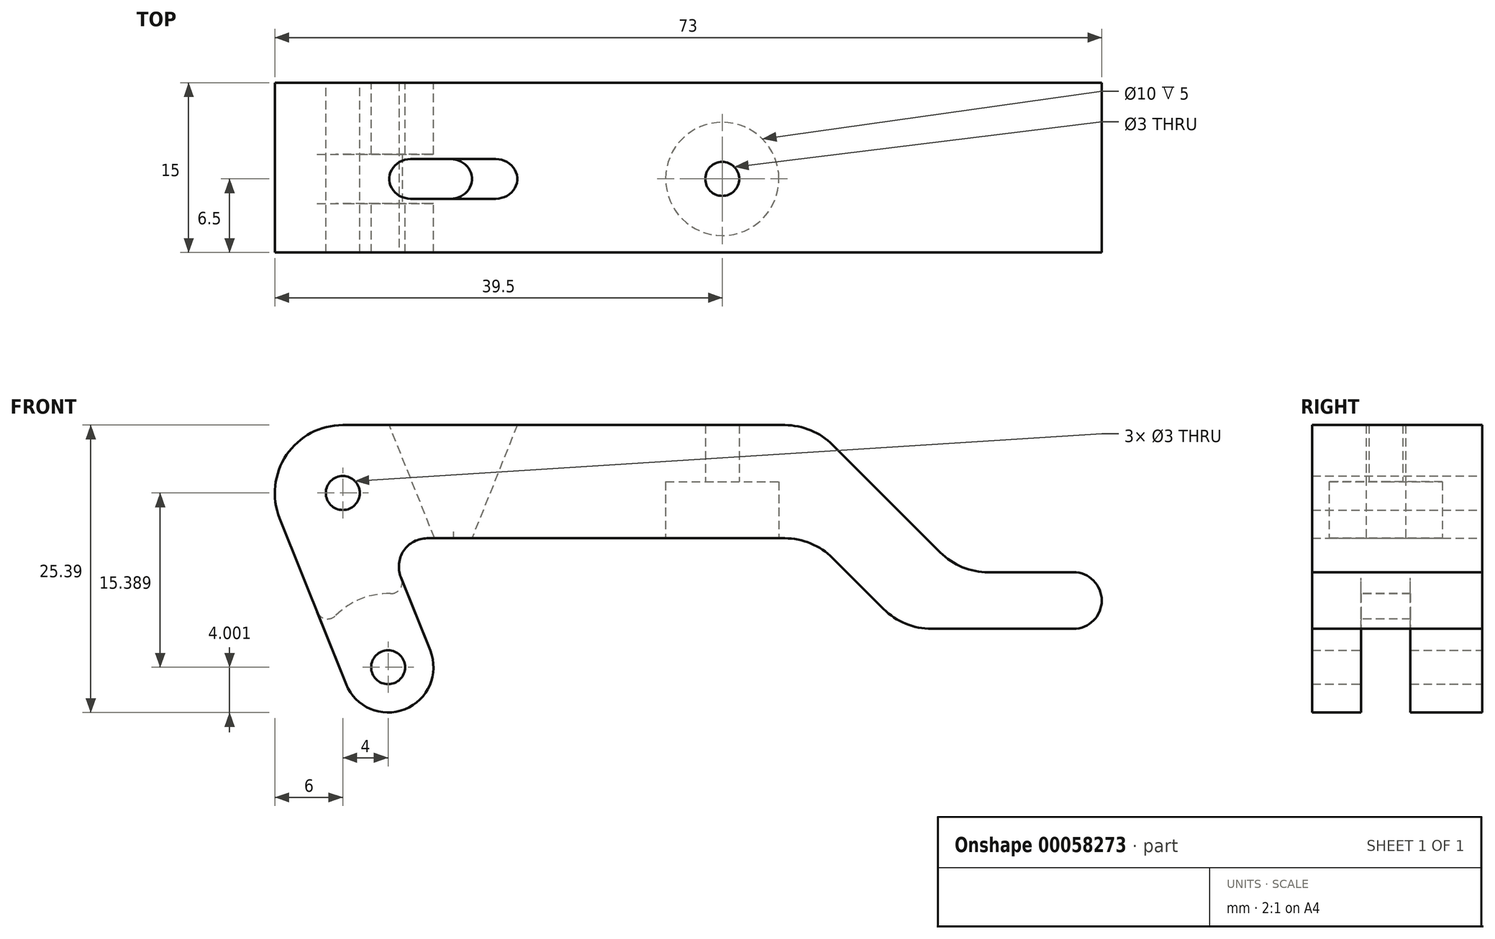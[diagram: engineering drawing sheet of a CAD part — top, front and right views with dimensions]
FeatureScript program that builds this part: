
annotation { "Feature Type Name" : "Feature", "Feature Type Description" : "" }
export const myFeature = defineFeature(function(context is Context, id is Id, definition is map)
    precondition{}
    {
        {
            var Q0;
            Q0=qCreatedBy(makeId("Front.planeOp"),FACE);
            var sketch = newSketch(context, id + "F0", { "sketchPlane" : qUnion([Q0])});
            skLineSegment(sketch, "E0", {"start": v(0, 0) * mm, "end": v(31, 0) * mm, "construction": true});
            skCircle(sketch, "E1", {"center": v(0, 0) * mm, "radius": 1.5 * mm});
            skLineSegment(sketch, "E2", {"start": v(0, 0) * mm, "end": v(4, -15.39) * mm, "construction": true});
            skCircle(sketch, "E3", {"center": v(4, -15.39) * mm, "radius": 1.5 * mm});
            skArc(sketch, "E4", {"start": v(-5.57, -2.23) * mm, "mid": v(-4.97, 3.36) * mm, "end": v(0, 6) * mm});
            skArc(sketch, "E5", {"start": v(0.29, -16.87) * mm, "mid": v(5.49, -19.1) * mm, "end": v(7.71, -13.9) * mm});
            skLineSegment(sketch, "E6", {"start": v(-5.57, -2.23) * mm, "end": v(0.29, -16.87) * mm});
            skLineSegment(sketch, "E7", {"start": v(0, 6) * mm, "end": v(41.5, 6) * mm});
            skLineSegment(sketch, "E8", {"start": v(41.5, 6) * mm, "end": v(54.5, -7) * mm});
            skLineSegment(sketch, "E9", {"start": v(54.5, -7) * mm, "end": v(67, -7) * mm});
            skLineSegment(sketch, "E10", {"start": v(15.5, 0) * mm, "end": v(15.5, -12.95) * mm, "construction": true});
            skLineSegment(sketch, "E11", {"start": v(9.75, 0) * mm, "end": v(9.75, -27.58) * mm, "construction": true});
            skLineSegment(sketch, "E12", {"start": v(7.71, -13.9) * mm, "end": v(3.75, -4) * mm});
            skLineSegment(sketch, "E13", {"start": v(3.75, -4) * mm, "end": v(41.5, -4) * mm});
            skLineSegment(sketch, "E14", {"start": v(41.5, -4) * mm, "end": v(49.5, -12) * mm});
            skLineSegment(sketch, "E15", {"start": v(49.5, -12) * mm, "end": v(67, -12) * mm});
            skLineSegment(sketch, "E16", {"start": v(67, -12) * mm, "end": v(67, -7) * mm});
            skSolve(sketch);
        }
        {
            var Q0;
            Q0=qSketchRegion(id+"F0",true);
            extrude(context, id + "F1", {"entities" : qUnion([Q0]), "depth" : 13 * mm, "symmetric" : true});
        }
        {
            var Q0;
            Q0=qCreatedBy(makeId("Front.planeOp"),FACE);
            var sketch = newSketch(context, id + "F2", { "sketchPlane" : qUnion([Q0])});
            skCircle(sketch, "E17.0", {"center": v(4, -15.39) * mm, "radius": 1.5 * mm, "construction": true});
            skCircle(sketch, "E18", {"center": v(4, -15.39) * mm, "radius": 6.5 * mm});
            skSolve(sketch);
        }
        {
            var Q0;
            Q0=qSketchRegion(id+"F2",true);
            extrude(context, id + "F3", {"entities" : qUnion([Q0]), "operationType" : NewBodyOperationType.REMOVE, "oppositeDirection" : true, "depth" : 4.35 * mm, "symmetric" : true});
        }
        {
            var Q0;
            Q0=qCreatedBy(makeId("Front.planeOp"),FACE);
            var sketch = newSketch(context, id + "F4", { "sketchPlane" : qUnion([Q0])});
            skLineSegment(sketch, "E19", {"start": v(0, 0) * mm, "end": v(15.5, 0) * mm, "construction": true});
            skLineSegment(sketch, "E20", {"start": v(9.75, 0) * mm, "end": v(9.75, -20.2) * mm, "construction": true});
            skPoint(sketch, "E21", {"position": v(6.5, 0) * mm});
            skLineSegment(sketch, "E22", {"start": v(8.5, 0) * mm, "end": v(8.5, -21.18) * mm, "construction": true});
            skLineSegment(sketch, "E23.0", {"start": v(0, 6) * mm, "end": v(41.5, 6) * mm, "construction": true});
            skLineSegment(sketch, "E23.1", {"start": v(3.75, -4) * mm, "end": v(41.5, -4) * mm, "construction": true});
            skLineSegment(sketch, "E24", {"start": v(4.1, 6) * mm, "end": v(8.1, -4) * mm});
            skLineSegment(sketch, "E25.MirrorCS", {"start": v(15.4, 6) * mm, "end": v(11.4, -4) * mm});
            skLineSegment(sketch, "E26", {"start": v(4.1, 6) * mm, "end": v(15.4, 6) * mm});
            skLineSegment(sketch, "E27", {"start": v(8.1, -4) * mm, "end": v(11.4, -4) * mm});
            skSolve(sketch);
        }
        {
            var Q0;
            Q0=qSketchRegion(id+"F4",true);
            extrude(context, id + "F5", {"entities" : qUnion([Q0]), "operationType" : NewBodyOperationType.REMOVE, "depth" : 3.5 * mm, "symmetric" : true});
        }
        {
            var Q0;
            Q0=makeQuery(id+"F1.opExtrude","SWEPT_EDGE",EDGE,{"disambiguationData":[OSD([sQuery(id+"F0.wireOp",EDGE,"E12"),sQuery(id+"F0.wireOp",EDGE,"E13")])]});
            var Q1;
            Q1=makeQuery(id+"F1.opExtrude","SWEPT_EDGE",EDGE,{"disambiguationData":[OSD([sQuery(id+"F0.wireOp",EDGE,"E9"),sQuery(id+"F0.wireOp",EDGE,"E16")])]});
            var Q2;
            Q2=makeQuery(id+"F1.opExtrude","SWEPT_EDGE",EDGE,{"disambiguationData":[OSD([sQuery(id+"F0.wireOp",EDGE,"E15"),sQuery(id+"F0.wireOp",EDGE,"E16")])]});
            fillet(context, id + "F6", {"entities" : qUnion([Q0, Q1, Q2]), "radius" : 2.5 * mm, "tangentPropagation" : true, "allowEdgeOverflow" : false});
        }
        {
            var Q0;
            Q0=makeQuery(id+"F5.boolean.opBoolean","COPY",EDGE,{"derivedFrom":makeQuery(id+"F5.opExtrude","CAP_EDGE",EDGE,{"disambiguationData":[OSD([sQuery(id+"F4.wireOp",EDGE,"E25.MirrorCS")])],"isStart":true})});
            var Q1;
            Q1=makeQuery(id+"F5.boolean.opBoolean","COPY",EDGE,{"derivedFrom":makeQuery(id+"F5.opExtrude","CAP_EDGE",EDGE,{"disambiguationData":[OSD([sQuery(id+"F4.wireOp",EDGE,"E24")])],"isStart":true})});
            var Q2;
            Q2=makeQuery(id+"F5.boolean.opBoolean","COPY",EDGE,{"derivedFrom":makeQuery(id+"F5.opExtrude","CAP_EDGE",EDGE,{"disambiguationData":[OSD([sQuery(id+"F4.wireOp",EDGE,"E25.MirrorCS")])],"isStart":false})});
            var Q3;
            Q3=makeQuery(id+"F5.boolean.opBoolean","COPY",EDGE,{"derivedFrom":makeQuery(id+"F5.opExtrude","CAP_EDGE",EDGE,{"disambiguationData":[OSD([sQuery(id+"F4.wireOp",EDGE,"E24")])],"isStart":false})});
            fillet(context, id + "F7", {"entities" : qUnion([Q0, Q1, Q2, Q3]), "radius" : 1.75 * mm, "tangentPropagation" : true, "allowEdgeOverflow" : false});
        }
        {
            var Q0;
            Q0=makeQuery(id+"F3.boolean.opBoolean","INTERSECT",EDGE,{"derivedFrom":[makeQuery(id+"F1.opExtrude","SWEPT_FACE",FACE,{"disambiguationData":[OSD([sQuery(id+"F0.wireOp",EDGE,"E6")])]}),makeQuery(id+"F3.opExtrude","SWEPT_FACE",FACE,{"disambiguationData":[OSD([sQuery(id+"F2.wireOp",EDGE,"E18")])]})]});
            var Q1;
            Q1=makeQuery(id+"F3.boolean.opBoolean","INTERSECT",EDGE,{"derivedFrom":[makeQuery(id+"F1.opExtrude","SWEPT_FACE",FACE,{"disambiguationData":[OSD([sQuery(id+"F0.wireOp",EDGE,"E12")])]}),makeQuery(id+"F3.opExtrude","SWEPT_FACE",FACE,{"disambiguationData":[OSD([sQuery(id+"F2.wireOp",EDGE,"E18")])]})]});
            fillet(context, id + "F8", {"entities" : qUnion([Q0, Q1]), "radius" : 1 * mm, "tangentPropagation" : true, "allowEdgeOverflow" : false});
        }
        {
            var Q0;
            Q0=makeQuery(id+"F1.opExtrude","SWEPT_EDGE",EDGE,{"disambiguationData":[OSD([sQuery(id+"F0.wireOp",EDGE,"E7"),sQuery(id+"F0.wireOp",EDGE,"E8")])]});
            var Q1;
            Q1=makeQuery(id+"F1.opExtrude","SWEPT_EDGE",EDGE,{"disambiguationData":[OSD([sQuery(id+"F0.wireOp",EDGE,"E8"),sQuery(id+"F0.wireOp",EDGE,"E9")])]});
            var Q2;
            Q2=makeQuery(id+"F1.opExtrude","SWEPT_EDGE",EDGE,{"disambiguationData":[OSD([sQuery(id+"F0.wireOp",EDGE,"E13"),sQuery(id+"F0.wireOp",EDGE,"E14")])]});
            var Q3;
            Q3=makeQuery(id+"F1.opExtrude","SWEPT_EDGE",EDGE,{"disambiguationData":[OSD([sQuery(id+"F0.wireOp",EDGE,"E14"),sQuery(id+"F0.wireOp",EDGE,"E15")])]});
            fillet(context, id + "F9", {"entities" : qUnion([Q0, Q1, Q2, Q3]), "radius" : 6 * mm, "tangentPropagation" : true, "allowEdgeOverflow" : false});
        }
        {
            var Q0;
            Q0=makeQuery(id+"F1.opExtrude","SWEPT_FACE",FACE,{"disambiguationData":[OSD([sQuery(id+"F0.wireOp",EDGE,"E13")])]});
            var sketch = newSketch(context, id + "F10", { "sketchPlane" : qUnion([Q0])});
            skLineSegment(sketch, "E28.0", {"start": v(-1.5, 6.5) * mm, "end": v(1.5, 6.5) * mm, "construction": true});
            skLineSegment(sketch, "E29", {"start": v(0, 6.5) * mm, "end": v(31, 6.5) * mm, "construction": true});
            skLineSegment(sketch, "E30", {"start": v(15.5, 6.5) * mm, "end": v(15.5, -6.5) * mm, "construction": true});
            skLineSegment(sketch, "E31", {"start": v(15.5, 0) * mm, "end": v(33.5, 0) * mm, "construction": true});
            skPoint(sketch, "E31.endSnap0", {"position": v(15.5, 0) * mm});
            skPoint(sketch, "E32", {"position": v(23, 0) * mm});
            skCircle(sketch, "E33", {"center": v(33.5, 0) * mm, "radius": 5 * mm});
            skSolve(sketch);
        }
        {
            var Q0;
            Q0=qSketchRegion(id+"F10",true);
            extrude(context, id + "F11", {"entities" : qUnion([Q0]), "operationType" : NewBodyOperationType.REMOVE, "oppositeDirection" : true, "depth" : 5 * mm});
        }
        {
            var Q0;
            Q0=makeQuery(id+"F1.opExtrude","CAP_FACE",FACE,{"disambiguationData":[OSD([sQuery(id+"F0.wireOp",EDGE,"E1"),sQuery(id+"F0.wireOp",EDGE,"E3"),sQuery(id+"F0.wireOp",EDGE,"E4"),sQuery(id+"F0.wireOp",EDGE,"E5"),sQuery(id+"F0.wireOp",EDGE,"E6"),sQuery(id+"F0.wireOp",EDGE,"E7"),sQuery(id+"F0.wireOp",EDGE,"E8"),sQuery(id+"F0.wireOp",EDGE,"E9"),sQuery(id+"F0.wireOp",EDGE,"E12"),sQuery(id+"F0.wireOp",EDGE,"E13"),sQuery(id+"F0.wireOp",EDGE,"E14"),sQuery(id+"F0.wireOp",EDGE,"E15"),sQuery(id+"F0.wireOp",EDGE,"E16")])],"isStart":true});
            extrude(context, id + "F12", {"entities" : qUnion([Q0]), "operationType" : NewBodyOperationType.ADD, "depth" : 2 * mm});
        }
        {
            var Q0;
            Q0=makeQuery(id+"F11.boolean.opBoolean","COPY",FACE,{"derivedFrom":makeQuery(id+"F11.opExtrude","CAP_FACE",FACE,{"disambiguationData":[OSD([sQuery(id+"F10.wireOp",EDGE,"E33")])],"isStart":false})});
            var sketch = newSketch(context, id + "F13", { "sketchPlane" : qUnion([Q0])});
            skCircle(sketch, "E34", {"center": v(33.5, 0) * mm, "radius": 1.5 * mm});
            skSolve(sketch);
        }
        {
            var Q0;
            Q0 = qSketchRegion(id + "F13", true);
            extrude(context, id + "F14", {"entities" : qUnion([Q0]), "operationType" : NewBodyOperationType.REMOVE, "endBound" : BoundingType.THROUGH_ALL, "oppositeDirection" : true, "depth" : 25 * mm});
        }
    });
